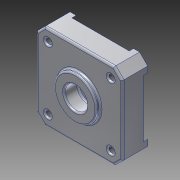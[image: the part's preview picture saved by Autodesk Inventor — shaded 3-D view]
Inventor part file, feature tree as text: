
AUTODESK INVENTOR PART (.ipt)
format: ipt  version: 2015 (Build 190159000, 159)  size: 225,280 bytes
history: native  units: mm
features: extrude x4, thread x4, sketch x4, hole x3, fillet x2, pattern_linear x1
ambient origin geometry x8: Origin, YZ Plane, XZ Plane, XY Plane, X Axis, Y Axis, Z Axis, Center Point
bodies: Solid1 (feature_tree)
feature tree (18):
  extrude  "Extrusion1"  Depth=42.3mm
  extrude  "Extrusion2"  Depth=10.5mm
  extrude  "Extrusion3"  Depth=10.5mm TaperAngle=0.0deg
  hole  "Hole1"  [1 undecoded]
  hole  "Hole2"  [1 undecoded]
  pattern_linear  "Rectangular Pattern1"  Spacing1=5.65mm  [1 undecoded]
  hole  "Hole3"  [1 undecoded]
  fillet  "Fillet1"  Radius=20.0mm
  extrude  "Extrusion4"  Depth=10.0mm
  fillet  "Fillet4"  Radius=1.0mm
  thread  "Thread1"  [1 undecoded]
  thread  "Thread2"  [1 undecoded]
  thread  "Thread3"  [1 undecoded]
  thread  "Thread4"  [1 undecoded]
  sketch  "Sketch1"  dims[d0=42.3mm d1=42.3mm]
  sketch  "Sketch2"  dims[d2=10.5mm d3=0.0mm d4=5.657mm]
  sketch  "Sketch3"  dims[d5=135.0deg d6=10.5mm d7=0.0mm]
  sketch  "Sketch4"  dims[d8=2.121mm d9=2.121mm d10=0.0mm d11=21.15mm d12=21.15mm d13=5.0mm d14=6.0mm d15=4.0mm d16=2.0mm d17=90.0deg d18=8.0mm d19=20.594885mm d20=5.65mm d21=5.65mm d22=3.0mm d23=6.0mm d24=4.0mm d25=2.0mm d26=90.0deg d27=8.0mm d28=20.594885mm d29=20.0mm d31=31.0mm d32=20.0mm d34=31.0mm d35=21.15mm d36=21.15mm d37=11.0mm d38=6.0mm d39=4.0mm d40=2.0mm d41=90.0deg d42=5.0mm d43=0.0mm d59=1.0mm d62=21.0mm d63=2.0mm d64=0.0mm d65=0.75mm d66=10.0mm d67=0.0mm d68=10.0mm d69=0.0mm d70=10.0mm d71=0.0mm d72=10.0mm d73=0.0mm]
note: 8 required parameter values undecoded (feature->parameter linkage not recoverable at this tier; creation-order binding heuristic only, values carry confidence <= 0.55)
